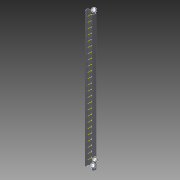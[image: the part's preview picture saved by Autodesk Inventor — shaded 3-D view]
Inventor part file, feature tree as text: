
AUTODESK INVENTOR PART (.ipt)
format: ipt  version: 2015 (Build 190159000, 159)  size: 439,296 bytes
history: native  units: in
note: dims shown in document units (in); Inventor stores cm internally (conversion verified against a paired STEP export)
features: other x28, boolean_combine x1, extrude x1, pattern_linear x1, plane x1, imported_body x1, sketch x1
ambient origin geometry x8: Origin, YZ Plane, XZ Plane, XY Plane, X Axis, Y Axis, Z Axis, Center Point
bodies: Body1 (feature_tree)
feature tree (34):
  boolean_combine  "Combine1"
  other  "Linear Slide"
  other  "Work Axis1"
  extrude  "Extrusion1"  TaperAngle=0.0deg  [1 undecoded]
  pattern_linear  "Rectangular Pattern1"  Spacing1=0.0in  [1 undecoded]
  plane  "Work Plane3"
  imported_body  "Base1"
  other  "Work Point1"
  other  "Work Axis2"
  sketch  "Sketch1"  dims[d0=9.8425in d2=0.5in d4=0.0in d5=0.0in d6=0.0in d9=-12.5in d10=0.0in]
  other  "Work Axis46"
  other  "Work Axis47"
  other  "Work Axis48"
  other  "Work Axis49"
  other  "Work Axis50"
  other  "Work Axis51"
  other  "Work Axis52"
  other  "Work Axis53"
  other  "Work Axis54"
  other  "Work Axis55"
  other  "Work Axis56"
  other  "Work Axis57"
  other  "Work Axis69"
  other  "Work Axis70"
  other  "Work Axis71"
  other  "Work Axis72"
  other  "Work Axis73"
  other  "Work Axis74"
  other  "Work Axis75"
  other  "Work Axis76"
  other  "Work Axis77"
  other  "Work Axis78"
  other  "bottom plane"
  other  "Work Axis90"
note: 2 required parameter values undecoded (feature->parameter linkage not recoverable at this tier; creation-order binding heuristic only, values carry confidence <= 0.55)
